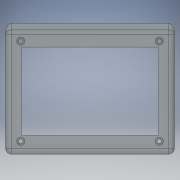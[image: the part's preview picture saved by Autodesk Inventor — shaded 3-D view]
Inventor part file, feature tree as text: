
AUTODESK INVENTOR PART (.ipt)
format: ipt  version: 2019 (Build 230136000, 136)  size: 247,296 bytes
history: native  units: mm
features: extrude x10, sketch x10, projected_geometry x3, other x1, imported_body x1
ambient origin geometry x8: Origin, YZ Plane, XZ Plane, XY Plane, X Axis, Y Axis, Z Axis, Center Point
bodies: Body1 (feature_tree)
feature tree (25):
  other  "實體1"
  extrude  "擠出1"  TaperAngle=0.0deg  [1 undecoded]
  extrude  "擠出2"  Depth=5.0mm TaperAngle=0.0deg
  extrude  "擠出3"  Depth=1.5mm TaperAngle=0.0deg
  extrude  "擠出4"  Depth=1.5mm TaperAngle=0.0deg
  extrude  "擠出5"  TaperAngle=0.0deg  [1 undecoded]
  extrude  "擠出7"  TaperAngle=0.0deg  [1 undecoded]
  extrude  "擠出8"  Depth=14.0mm
  extrude  "擠出9"  Depth=20.0mm
  extrude  "擠出10"  Depth=3.0mm TaperAngle=0.0deg
  extrude  "擠出11"  Depth=2.5mm TaperAngle=0.0deg
  sketch  "草圖2"
  sketch  "草圖3"
  projected_geometry  "投影迴路1"
  sketch  "草圖4"
  sketch  "草圖5"
  projected_geometry  "投影迴路2"
  sketch  "草圖7"
  sketch  "草圖10"
  sketch  "草圖11"
  sketch  "草圖12"
  sketch  "草圖13"
  sketch  "草圖14"
  projected_geometry  "投影迴路4"
  imported_body  "Base1"
note: 3 required parameter values undecoded (feature->parameter linkage not recoverable at this tier; creation-order binding heuristic only, values carry confidence <= 0.55)
